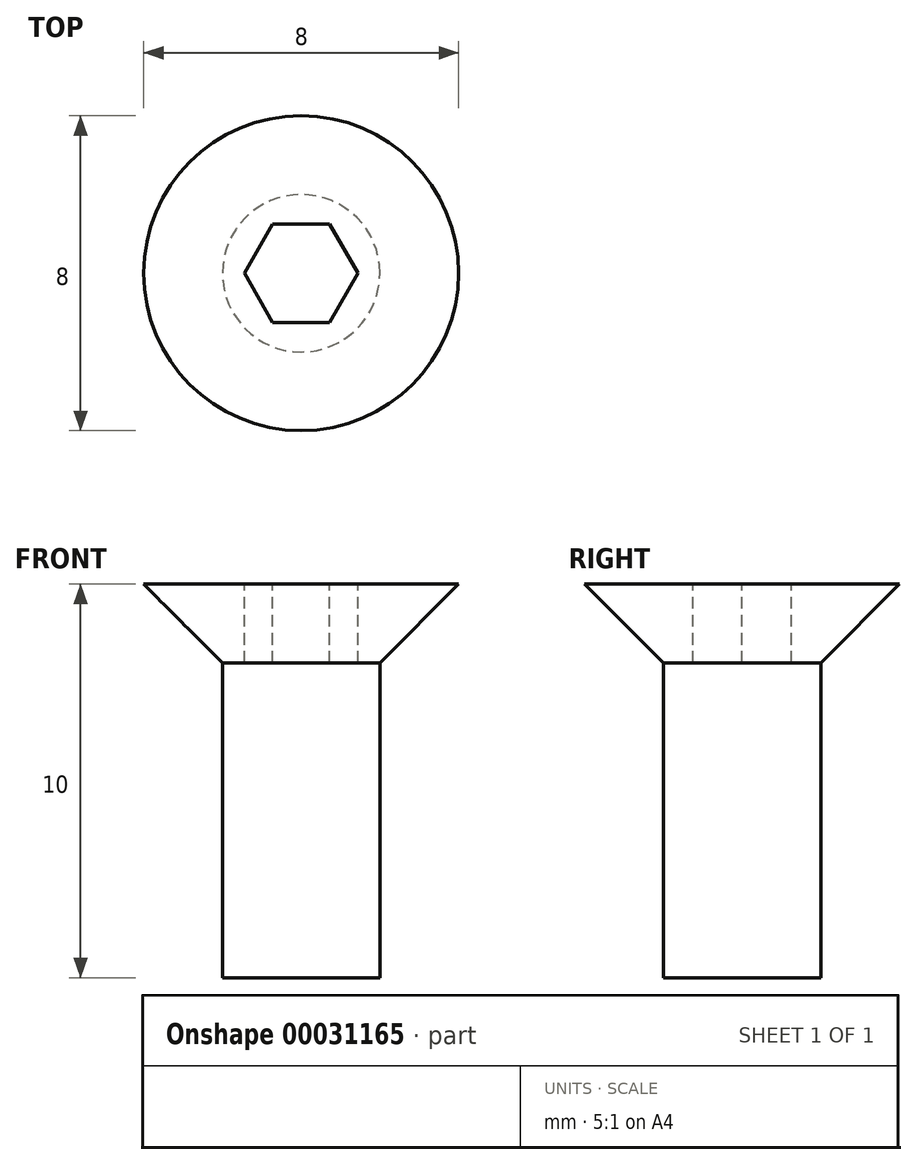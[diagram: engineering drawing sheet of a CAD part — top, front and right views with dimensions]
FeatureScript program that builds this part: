
annotation { "Feature Type Name" : "Feature", "Feature Type Description" : "" }
export const myFeature = defineFeature(function(context is Context, id is Id, definition is map)
    precondition{}
    {
        {
            var Q0;
            Q0=qCreatedBy(makeId("Front.planeOp"),FACE);
            var sketch = newSketch(context, id + "F0", { "sketchPlane" : qUnion([Q0])});
            skLineSegment(sketch, "E0", {"start": v(0, 0) * mm, "end": v(4, 0) * mm});
            skLineSegment(sketch, "E1", {"start": v(4, 0) * mm, "end": v(2, -2) * mm});
            skLineSegment(sketch, "E2", {"start": v(2, -2) * mm, "end": v(2, -10) * mm});
            skLineSegment(sketch, "E3", {"start": v(2, -10) * mm, "end": v(0, -10) * mm});
            skLineSegment(sketch, "E4", {"start": v(0, -10) * mm, "end": v(0, 0) * mm});
            skSolve(sketch);
        }
        {
            var Q0;
            Q0=makeQuery(id+"F0.imprint","IMPRINT",FACE,{"disambiguationData":[TD([[makeQuery(id+"F0.imprint","IMPRINT",EDGE,{"derivedFrom":sQuery(id+"F0.wireOp",EDGE,"E0")}),-1.0]])]});
            var Q1;
            Q1=sQuery(id+"F0.wireOp",EDGE,"E4");
            revolve(context, id + "F1", {"entities" : qUnion([Q0]), "axis" : qUnion([Q1]), "revolveType" : RevolveType.FULL});
        }
        {
            var Q0;
            Q0=makeQuery(id+"F1.opRevolve","SWEPT_FACE",FACE,{"disambiguationData":[OSD([sQuery(id+"F0.wireOp",EDGE,"E0")])]});
            var sketch = newSketch(context, id + "F2", { "sketchPlane" : qUnion([Q0])});
            skCircle(sketch, "E5.cCircle", {"center": v(0, 0) * mm, "radius": 1.25 * mm, "construction": true});
            skLineSegment(sketch, "E5.0", {"start": v(-0.72, 1.25) * mm, "end": v(0.72, 1.25) * mm});
            skLineSegment(sketch, "E5.1", {"start": v(0.72, 1.25) * mm, "end": v(1.44, 0) * mm});
            skLineSegment(sketch, "E5.2", {"start": v(1.44, 0) * mm, "end": v(0.72, -1.25) * mm});
            skLineSegment(sketch, "E5.3", {"start": v(0.72, -1.25) * mm, "end": v(-0.72, -1.25) * mm});
            skLineSegment(sketch, "E5.4", {"start": v(-0.72, -1.25) * mm, "end": v(-1.44, 0) * mm});
            skLineSegment(sketch, "E5.5", {"start": v(-1.44, 0) * mm, "end": v(-0.72, 1.25) * mm});
            skPoint(sketch, "E5.0.midPoint", {"position": v(0, 1.25) * mm});
            skSolve(sketch);
        }
        {
            var Q0;
            Q0=qSketchRegion(id+"F2",true);
            extrude(context, id + "F3", {"entities" : qUnion([Q0]), "operationType" : NewBodyOperationType.REMOVE, "oppositeDirection" : true, "depth" : 2 * mm});
        }
    });
